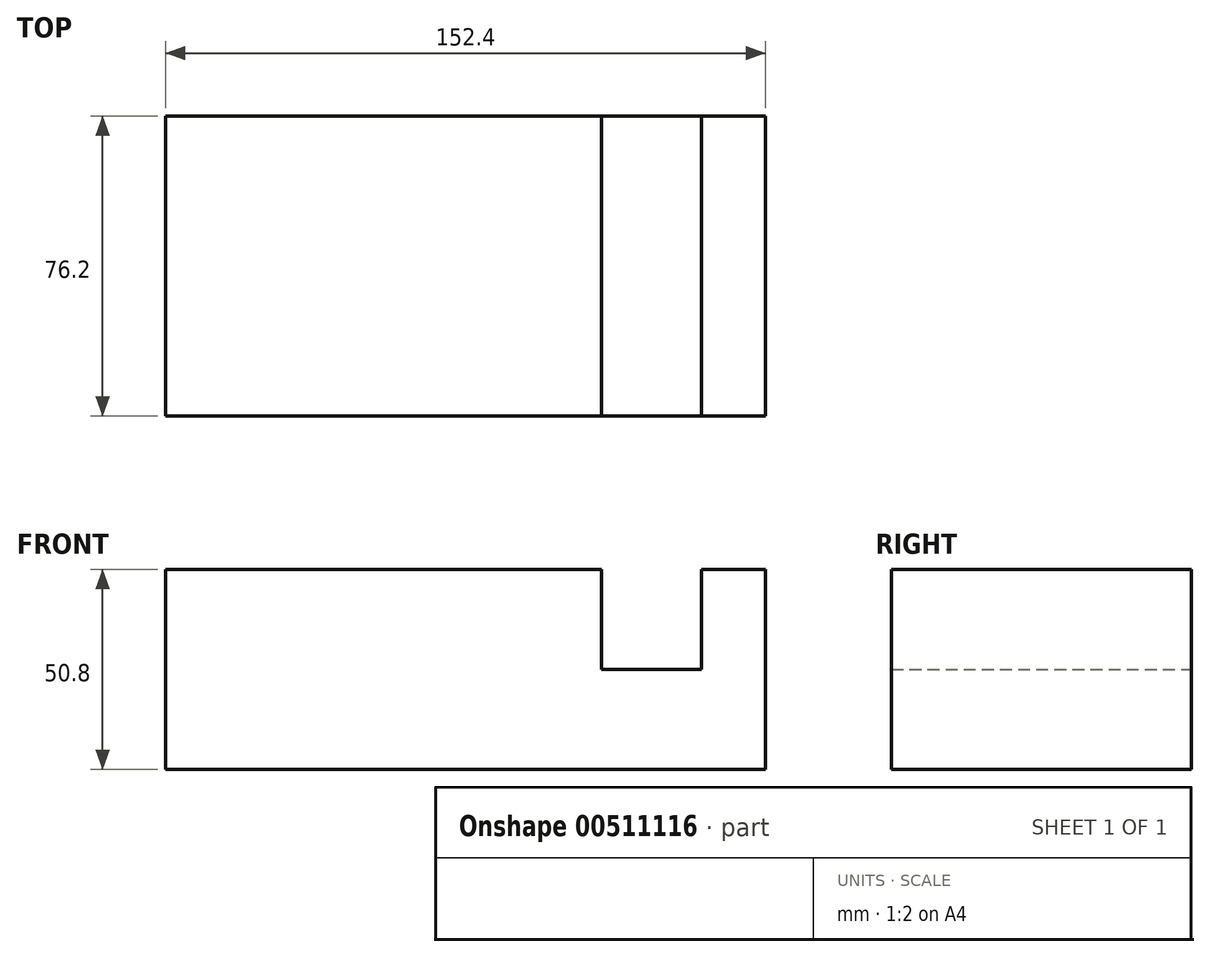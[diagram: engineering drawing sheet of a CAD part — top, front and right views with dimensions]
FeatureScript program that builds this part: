
annotation { "Feature Type Name" : "Feature", "Feature Type Description" : "" }
export const myFeature = defineFeature(function(context is Context, id is Id, definition is map)
    precondition{}
    {
        {
            var Q0;
            Q0=qCreatedBy(makeId("Front.planeOp"),FACE);
            var sketch = newSketch(context, id + "F0", { "sketchPlane" : qUnion([Q0])});
            skLineSegment(sketch, "E0", {"start": v(-59.96, 50.8) * mm, "end": v(-59.96, 0) * mm});
            skLineSegment(sketch, "E1", {"start": v(-59.96, 50.8) * mm, "end": v(50.75, 50.8) * mm});
            skLineSegment(sketch, "E2", {"start": v(50.75, 50.8) * mm, "end": v(50.75, 25.4) * mm});
            skLineSegment(sketch, "E3", {"start": v(50.75, 25.4) * mm, "end": v(76.15, 25.4) * mm});
            skLineSegment(sketch, "E4", {"start": v(76.15, 25.4) * mm, "end": v(76.15, 50.8) * mm});
            skLineSegment(sketch, "E5", {"start": v(76.15, 50.8) * mm, "end": v(92.44, 50.8) * mm});
            skLineSegment(sketch, "E6", {"start": v(92.44, 50.8) * mm, "end": v(92.44, 0) * mm});
            skLineSegment(sketch, "E7", {"start": v(-59.96, 0) * mm, "end": v(92.44, 0) * mm});
            skSolve(sketch);
        }
        {
            var Q0;
            Q0 = qSketchRegion(id + "F0", true);
            extrude(context, id + "F1", {"entities" : qUnion([Q0]), "depth" : 76.2 * mm});
        }
    });
